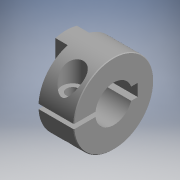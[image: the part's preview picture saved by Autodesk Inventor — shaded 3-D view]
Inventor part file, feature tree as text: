
AUTODESK INVENTOR PART (.ipt)
format: ipt  version: 2017.3 (Build 213256000, 256)  size: 168,960 bytes
history: native  units: mm (DEFAULTED — no unit token found)
features: other x14, sketch x7, extrude x3, revolve x2, hole x2
ambient origin geometry x8: Origin, YZ Plane, XZ Plane, XY Plane, X Axis, Y Axis, Z Axis, Center Point
bodies: Solid1 (feature_tree)
feature tree (28):
  revolve  "Revolution1"  [1 undecoded]
  extrude  "Extrusion1"  Depth=4.0mm TaperAngle=0.0deg
  revolve  "Revolution2"  [1 undecoded]
  hole  "Hole1"  [1 undecoded]
  extrude  "Extrusion2"  [1 undecoded]
  hole  "Hole2"  [1 undecoded]
  extrude  "Extrusion3"  [1 undecoded]
  other  "L_XY"
  other  "L_YZ"
  other  "L_ZX"
  other  "L_X"
  other  "L_Y"
  other  "L_Z"
  other  "L_Center"
  other  "screw_XY"
  other  "screw_YZ"
  other  "screw_ZX"
  other  "screw_X"
  other  "screw_Y"
  other  "screw_Z"
  other  "screw_Center"
  sketch  "Sketch_1"  dims[d0=360.0deg d1=11.5mm d2=0.0mm]
  sketch  "Sketch_6"  dims[d13=13.0mm d14=6.0mm d15=4.0mm d16=2.0mm d17=90.0deg d18=4.0mm d19=0.0mm d20=31.0mm d21=0.0mm]
  sketch  "Sketch_7"
  sketch  "Sketch4"  dims[d4=3.242mm d5=7.05mm d6=4.0mm d7=2.0mm d8=90.0deg d9=12.25mm d10=0.0mm d11=4.0mm d12=0.0mm]
  sketch  "Sketch_2"  dims[d3=360.0deg]
  sketch  "Sketch6"  dims[d22=0.0mm]
  sketch  "Sketch_15"
note: 6 required parameter values undecoded (feature->parameter linkage not recoverable at this tier; creation-order binding heuristic only, values carry confidence <= 0.55)